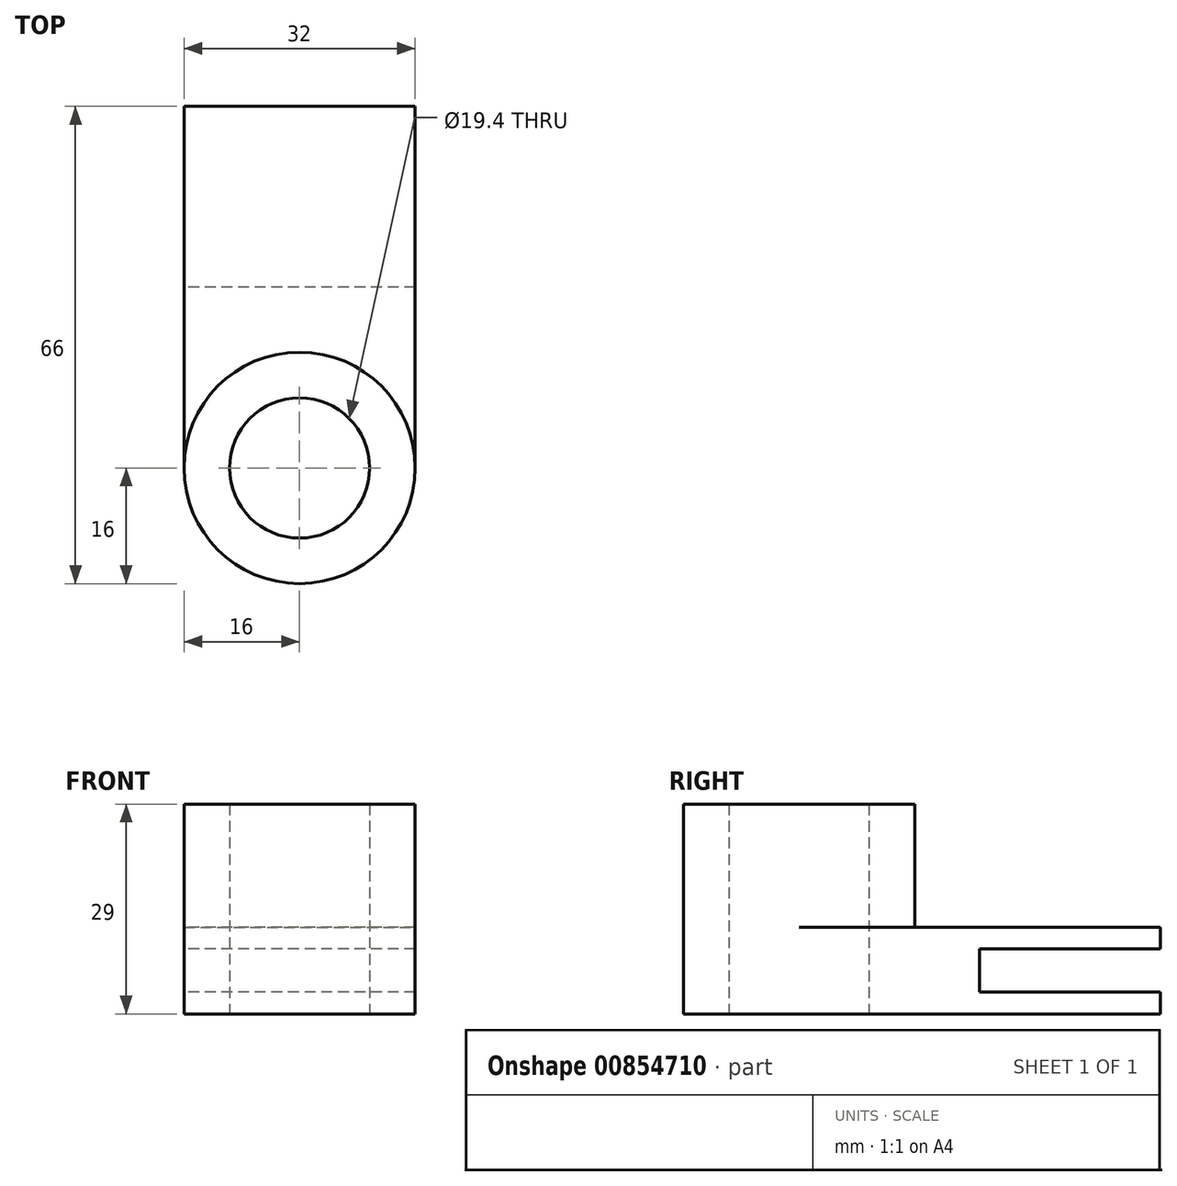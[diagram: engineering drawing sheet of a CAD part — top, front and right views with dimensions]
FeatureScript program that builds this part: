
annotation { "Feature Type Name" : "Feature", "Feature Type Description" : "" }
export const myFeature = defineFeature(function(context is Context, id is Id, definition is map)
    precondition{}
    {
        {
            var Q0;
            Q0=qCreatedBy(makeId("Top.planeOp"),FACE);
            var sketch = newSketch(context, id + "F0", { "sketchPlane" : qUnion([Q0])});
            skCircle(sketch, "E0", {"center": v(0, 0) * mm, "radius": 9.7 * mm});
            skCircle(sketch, "E1", {"center": v(0, 0) * mm, "radius": 16 * mm});
            skSolve(sketch);
        }
        {
            var Q0;
            Q0 = qSketchRegion(id + "F0", true);
            extrude(context, id + "F1", {"entities" : qUnion([Q0]), "depth" : 29 * mm, "offsetDistance" : 25 * mm});
        }
        {
            var Q0;
            Q0=qCreatedBy(makeId("Top.planeOp"),FACE);
            var sketch = newSketch(context, id + "F2", { "sketchPlane" : qUnion([Q0])});
            skLineSegment(sketch, "E2", {"start": v(-16, 0) * mm, "end": v(-16, 50) * mm});
            skLineSegment(sketch, "E3", {"start": v(-16, 50) * mm, "end": v(16, 50) * mm});
            skLineSegment(sketch, "E4", {"start": v(16, 50) * mm, "end": v(16, 0) * mm});
            skCircle(sketch, "E5", {"center": v(0, 0) * mm, "radius": 16 * mm});
            skCircle(sketch, "E6", {"center": v(0, 0) * mm, "radius": 9.75 * mm});
            skSolve(sketch);
        }
        {
            var Q0;
            Q0 = qSketchRegion(id + "F2", true);
            extrude(context, id + "F3", {"entities" : qUnion([Q0]), "operationType" : NewBodyOperationType.ADD, "depth" : 12 * mm, "offsetDistance" : 25 * mm});
        }
        {
            var Q0;
            Q0=makeQuery(id+"F3.opExtrude","SWEPT_FACE",FACE,{"disambiguationData":[OSD([sQuery(id+"F2.wireOp",EDGE,"E3")])]});
            var sketch = newSketch(context, id + "F4", { "sketchPlane" : qUnion([Q0])});
            skLineSegment(sketch, "E7.bottom", {"start": v(-16, 9) * mm, "end": v(16, 9) * mm});
            skLineSegment(sketch, "E7.top", {"start": v(-16, 3) * mm, "end": v(16, 3) * mm});
            skLineSegment(sketch, "E7.left", {"start": v(-16, 9) * mm, "end": v(-16, 3) * mm});
            skLineSegment(sketch, "E7.right", {"start": v(16, 9) * mm, "end": v(16, 3) * mm});
            skSolve(sketch);
        }
        {
            var Q0;
            Q0 = qSketchRegion(id + "F4", true);
            extrude(context, id + "F5", {"entities" : qUnion([Q0]), "operationType" : NewBodyOperationType.REMOVE, "oppositeDirection" : true, "depth" : 25 * mm, "offsetDistance" : 25 * mm});
        }
    });
